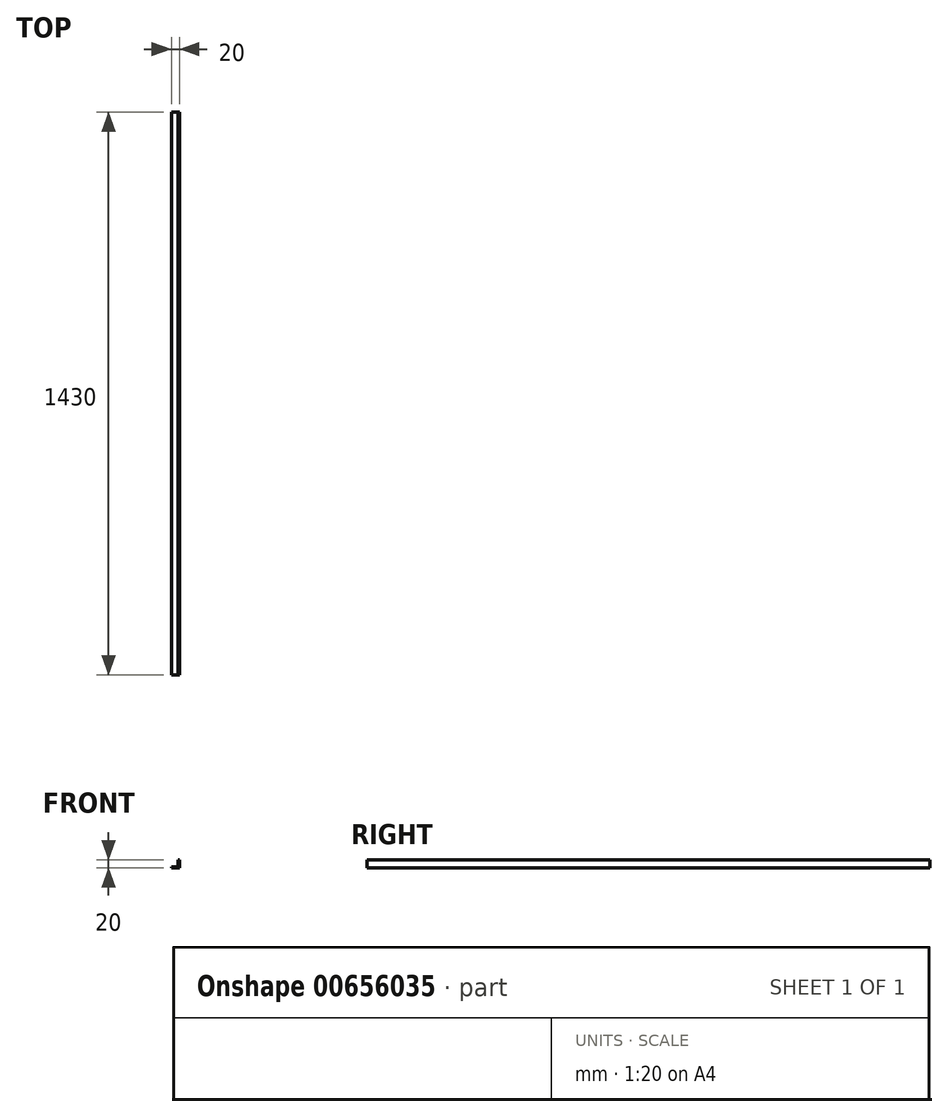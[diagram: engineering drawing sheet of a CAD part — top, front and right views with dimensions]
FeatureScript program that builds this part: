
annotation { "Feature Type Name" : "Feature", "Feature Type Description" : "" }
export const myFeature = defineFeature(function(context is Context, id is Id, definition is map)
    precondition{}
    {
        {
            var Q0;
            Q0=qCreatedBy(makeId("Front.planeOp"),FACE);
            var sketch = newSketch(context, id + "F0", { "sketchPlane" : qUnion([Q0])});
            skLineSegment(sketch, "E0", {"start": v(0, 0) * mm, "end": v(0, 17) * mm});
            skLineSegment(sketch, "E1", {"start": v(0, 17) * mm, "end": v(3, 17) * mm});
            skLineSegment(sketch, "E2", {"start": v(3, 17) * mm, "end": v(3, -3) * mm});
            skLineSegment(sketch, "E3", {"start": v(3, -3) * mm, "end": v(-17, -3) * mm});
            skLineSegment(sketch, "E4", {"start": v(-17, -3) * mm, "end": v(-17, 0) * mm});
            skLineSegment(sketch, "E5", {"start": v(-17, 0) * mm, "end": v(0, 0) * mm});
            skSolve(sketch);
        }
        {
            var Q0;
            Q0=makeQuery(id+"F0.imprint","IMPRINT",FACE,{"disambiguationData":[TD([[makeQuery(id+"F0.imprint","IMPRINT",EDGE,{"derivedFrom":sQuery(id+"F0.wireOp",EDGE,"E0")}),-1.0]])]});
            extrude(context, id + "F1", {"entities" : qUnion([Q0]), "depth" : 1430 * mm, "offsetDistance" : 25.4 * mm});
        }
    });
